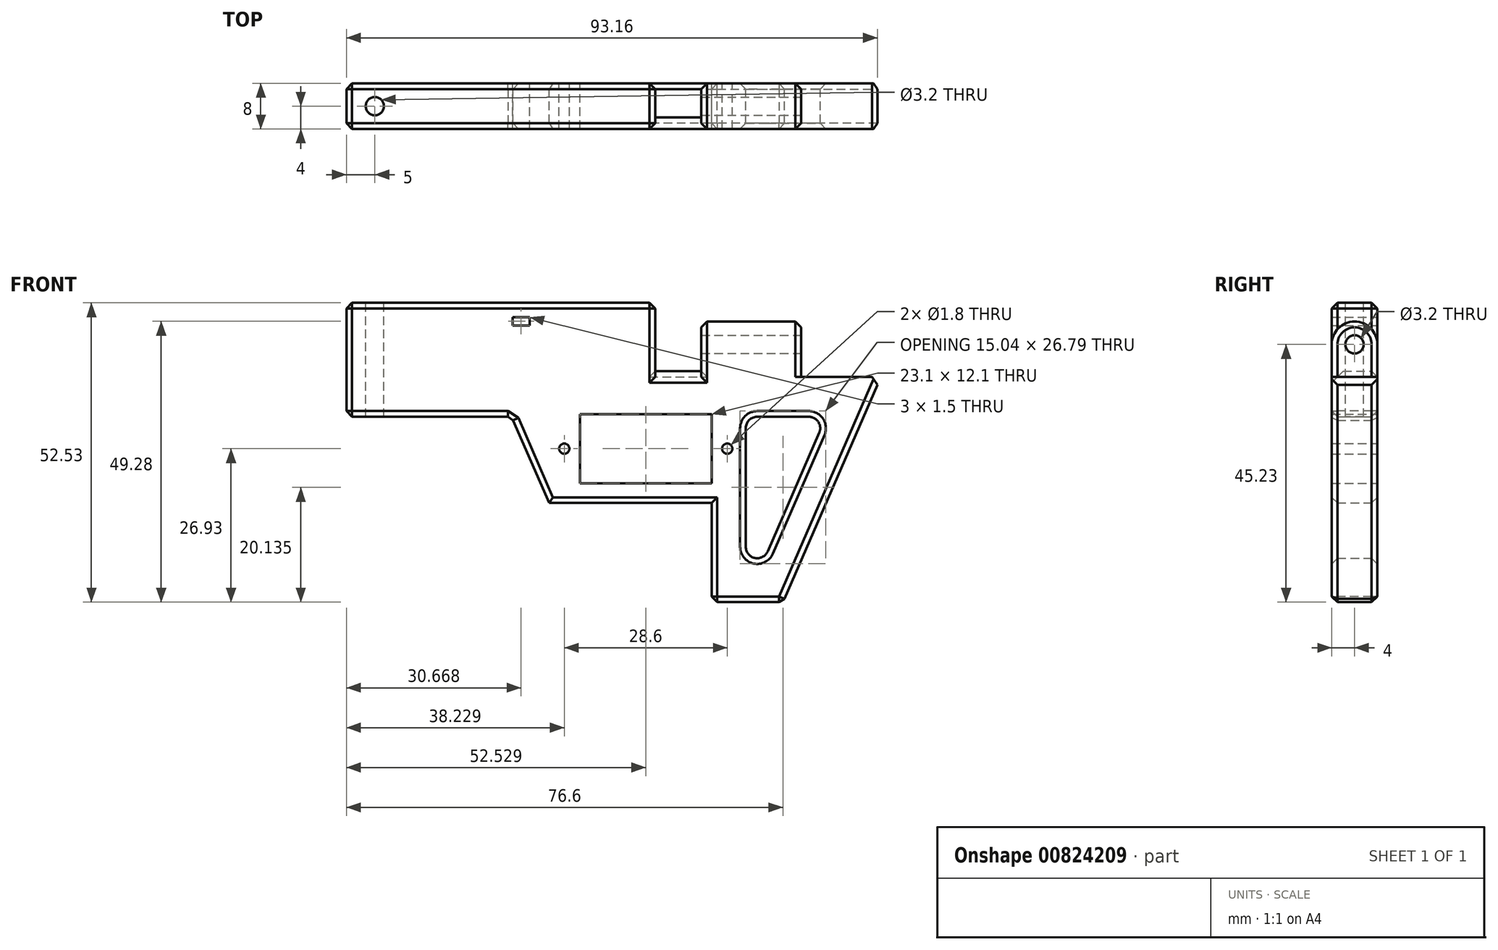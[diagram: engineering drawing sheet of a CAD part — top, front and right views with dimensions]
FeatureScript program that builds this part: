
annotation { "Feature Type Name" : "Feature", "Feature Type Description" : "" }
export const myFeature = defineFeature(function(context is Context, id is Id, definition is map)
    precondition{}
    {
        {
            var Q0;
            Q0=qCreatedBy(makeId("Front.planeOp"),FACE);
            var sketch = newSketch(context, id + "F0", { "sketchPlane" : qUnion([Q0])});
            skLineSegment(sketch, "E0", {"start": v(0, 0) * mm, "end": v(29, 0) * mm});
            skLineSegment(sketch, "E1", {"start": v(29, 0) * mm, "end": v(35.58, -15.13) * mm});
            skLineSegment(sketch, "E2", {"start": v(35.58, -15.13) * mm, "end": v(64.08, -15.13) * mm});
            skLineSegment(sketch, "E3", {"start": v(64.08, -15.13) * mm, "end": v(64.08, -32.53) * mm});
            skLineSegment(sketch, "E4", {"start": v(64.08, -32.53) * mm, "end": v(76.58, -32.53) * mm});
            skLineSegment(sketch, "E5", {"start": v(76.58, -32.53) * mm, "end": v(93.77, 7) * mm});
            skLineSegment(sketch, "E6", {"start": v(79.77, 7) * mm, "end": v(79.77, 16.7) * mm});
            skLineSegment(sketch, "E7", {"start": v(79.77, 16.7) * mm, "end": v(62.27, 16.7) * mm});
            skLineSegment(sketch, "E8", {"start": v(62.27, 16.7) * mm, "end": v(62.27, 8) * mm});
            skLineSegment(sketch, "E9", {"start": v(62.27, 8) * mm, "end": v(54.17, 8) * mm});
            skLineSegment(sketch, "E10", {"start": v(54.17, 8) * mm, "end": v(54.17, 20) * mm});
            skLineSegment(sketch, "E11", {"start": v(54.17, 20) * mm, "end": v(0, 20) * mm});
            skLineSegment(sketch, "E12", {"start": v(0, 20) * mm, "end": v(0, 0) * mm});
            skCircle(sketch, "E13", {"center": v(38.23, -5.6) * mm, "radius": 0.9 * mm});
            skCircle(sketch, "E14", {"center": v(66.83, -5.6) * mm, "radius": 0.9 * mm});
            skLineSegment(sketch, "E15.bottom", {"start": v(40.98, 0.45) * mm, "end": v(64.08, 0.45) * mm});
            skLineSegment(sketch, "E15.top", {"start": v(40.98, -11.65) * mm, "end": v(64.08, -11.65) * mm});
            skLineSegment(sketch, "E15.left", {"start": v(40.98, 0.45) * mm, "end": v(40.98, -11.65) * mm});
            skLineSegment(sketch, "E15.right", {"start": v(64.08, 0.45) * mm, "end": v(64.08, -11.65) * mm});
            skLineSegment(sketch, "E16", {"start": v(70.08, -2) * mm, "end": v(70.08, -22.82) * mm});
            skLineSegment(sketch, "E17", {"start": v(73.91, -23.62) * mm, "end": v(82.97, -2.8) * mm});
            skLineSegment(sketch, "E18", {"start": v(81.13, 0) * mm, "end": v(72.08, 0) * mm});
            skLineSegment(sketch, "E19.bottom", {"start": v(29.17, 17.5) * mm, "end": v(32.17, 17.5) * mm});
            skLineSegment(sketch, "E19.top", {"start": v(29.17, 16) * mm, "end": v(32.17, 16) * mm});
            skLineSegment(sketch, "E19.left", {"start": v(29.17, 17.5) * mm, "end": v(29.17, 16) * mm});
            skLineSegment(sketch, "E19.right", {"start": v(32.17, 17.5) * mm, "end": v(32.17, 16) * mm});
            skPoint(sketch, "E20.visualSharp", {"position": v(84.18, 0) * mm});
            skArc(sketch, "E20.filletArc", {"start": v(82.97, -2.8) * mm, "mid": v(82.8, -0.9) * mm, "end": v(81.13, 0) * mm});
            skPoint(sketch, "E21.visualSharp", {"position": v(70.08, 0) * mm});
            skArc(sketch, "E21.filletArc", {"start": v(72.08, 0) * mm, "mid": v(70.67, -0.59) * mm, "end": v(70.08, -2) * mm});
            skPoint(sketch, "E22.visualSharp", {"position": v(70.08, -32.43) * mm});
            skArc(sketch, "E22.filletArc", {"start": v(70.08, -22.82) * mm, "mid": v(71.67, -24.78) * mm, "end": v(73.91, -23.62) * mm});
            skPoint(sketch, "E23", {"position": v(40.98, -5.6) * mm});
            skLineSegment(sketch, "E24", {"start": v(52.53, 0.45) * mm, "end": v(52.53, -11.65) * mm, "construction": true});
            skLineSegment(sketch, "E25", {"start": v(93.77, 7) * mm, "end": v(79.77, 7) * mm});
            skPoint(sketch, "E26", {"position": v(49.83, -15.13) * mm});
            skSolve(sketch);
        }
        {
            var Q0;
            Q0=makeQuery(id+"F0.imprint","IMPRINT",FACE,{"disambiguationData":[TD([[makeQuery(id+"F0.imprint","IMPRINT",EDGE,{"derivedFrom":sQuery(id+"F0.wireOp",EDGE,"E0")}),1.0]])]});
            extrude(context, id + "F1", {"entities" : qUnion([Q0]), "depth" : 8 * mm, "offsetDistance" : 25 * mm});
        }
        {
            var Q0;
            Q0=makeQuery(id+"F1.opExtrude","SWEPT_FACE",FACE,{"disambiguationData":[OSD([sQuery(id+"F0.wireOp",EDGE,"E6")])]});
            var sketch = newSketch(context, id + "F2", { "sketchPlane" : qUnion([Q0])});
            skCircle(sketch, "E27", {"center": v(-4, 12.7) * mm, "radius": 1.6 * mm});
            skPoint(sketch, "E27.centerSnap0", {"position": v(-4, 16.7) * mm});
            skSolve(sketch);
        }
        {
            var Q0;
            Q0=makeQuery(id+"F2.imprint","IMPRINT",FACE,{"disambiguationData":[TD([[makeQuery(id+"F2.imprint","IMPRINT",EDGE,{"derivedFrom":sQuery(id+"F2.wireOp",EDGE,"E27")}),1.0]])]});
            extrude(context, id + "F3", {"entities" : qUnion([Q0]), "operationType" : NewBodyOperationType.REMOVE, "endBound" : BoundingType.UP_TO_NEXT, "oppositeDirection" : true, "depth" : 25 * mm, "offsetDistance" : 25 * mm});
        }
        {
            var Q0;
            Q0=makeQuery(id+"F1.opExtrude","CAP_EDGE",EDGE,{"disambiguationData":[OSD([sQuery(id+"F0.wireOp",EDGE,"E7")])],"isStart":false});
            var Q1;
            Q1=makeQuery(id+"F1.opExtrude","CAP_EDGE",EDGE,{"disambiguationData":[OSD([sQuery(id+"F0.wireOp",EDGE,"E7")])],"isStart":true});
            fillet(context, id + "F4", {"entities" : qUnion([Q0, Q1]), "radius" : 4 * mm, "tangentPropagation" : true, "allowEdgeOverflow" : false});
        }
        {
            var Q0;
            Q0=makeQuery(id+"F1.opExtrude","SWEPT_FACE",FACE,{"disambiguationData":[OSD([sQuery(id+"F0.wireOp",EDGE,"E11")])]});
            var sketch = newSketch(context, id + "F5", { "sketchPlane" : qUnion([Q0])});
            skCircle(sketch, "E28", {"center": v(5, -4) * mm, "radius": 1.6 * mm});
            skPoint(sketch, "E28.centerSnap0", {"position": v(0, -4) * mm});
            skSolve(sketch);
        }
        {
            var Q0;
            Q0 = qSketchRegion(id + "F5", true);
            extrude(context, id + "F6", {"entities" : qUnion([Q0]), "operationType" : NewBodyOperationType.REMOVE, "endBound" : BoundingType.UP_TO_NEXT, "oppositeDirection" : true, "depth" : 25 * mm, "offsetDistance" : 25 * mm});
        }
        {
            var Q0;
            Q0=makeQuery(id+"F1.opExtrude","CAP_EDGE",EDGE,{"disambiguationData":[OSD([sQuery(id+"F0.wireOp",EDGE,"E11")])],"isStart":true});
            var Q1;
            Q1=makeQuery(id+"F1.opExtrude","CAP_EDGE",EDGE,{"disambiguationData":[OSD([sQuery(id+"F0.wireOp",EDGE,"E10")])],"isStart":true});
            var Q2;
            Q2=makeQuery(id+"F1.opExtrude","CAP_EDGE",EDGE,{"disambiguationData":[OSD([sQuery(id+"F0.wireOp",EDGE,"E9")])],"isStart":true});
            var Q3;
            Q3=makeQuery(id+"F1.opExtrude","CAP_EDGE",EDGE,{"disambiguationData":[OSD([sQuery(id+"F0.wireOp",EDGE,"E8")])],"isStart":true});
            var Q4;
            Q4=makeQuery(id+"F1.opExtrude","CAP_EDGE",EDGE,{"disambiguationData":[OSD([sQuery(id+"F0.wireOp",EDGE,"E6")])],"isStart":true});
            var Q5;
            Q5=makeQuery(id+"F1.opExtrude","CAP_EDGE",EDGE,{"disambiguationData":[OSD([sQuery(id+"F0.wireOp",EDGE,"ISF7o4jE-YCiz-FvaA-wAcF-tz2zpi0BwcWr")])],"isStart":true});
            var Q6;
            Q6=makeQuery(id+"F1.opExtrude","CAP_EDGE",EDGE,{"disambiguationData":[OSD([sQuery(id+"F0.wireOp",EDGE,"E5")])],"isStart":false});
            var Q7;
            Q7=makeQuery(id+"F1.opExtrude","CAP_EDGE",EDGE,{"disambiguationData":[OSD([sQuery(id+"F0.wireOp",EDGE,"E17")])],"isStart":true});
            var Q8;
            Q8=makeQuery(id+"F1.opExtrude","CAP_EDGE",EDGE,{"disambiguationData":[OSD([sQuery(id+"F0.wireOp",EDGE,"E4")])],"isStart":true});
            var Q9;
            Q9=makeQuery(id+"F1.opExtrude","CAP_EDGE",EDGE,{"disambiguationData":[OSD([sQuery(id+"F0.wireOp",EDGE,"E2")])],"isStart":true});
            var Q10;
            Q10=makeQuery(id+"F1.opExtrude","CAP_EDGE",EDGE,{"disambiguationData":[OSD([sQuery(id+"F0.wireOp",EDGE,"E3")])],"isStart":true});
            var Q11;
            Q11=makeQuery(id+"F1.opExtrude","CAP_EDGE",EDGE,{"disambiguationData":[OSD([sQuery(id+"F0.wireOp",EDGE,"E1")])],"isStart":true});
            var Q12;
            Q12=makeQuery(id+"F1.opExtrude","CAP_EDGE",EDGE,{"disambiguationData":[OSD([sQuery(id+"F0.wireOp",EDGE,"E0")])],"isStart":true});
            var Q13;
            Q13=makeQuery(id+"F1.opExtrude","CAP_EDGE",EDGE,{"disambiguationData":[OSD([sQuery(id+"F0.wireOp",EDGE,"E12")])],"isStart":true});
            var Q14;
            Q14=makeQuery(id+"F1.opExtrude","SWEPT_EDGE",EDGE,{"disambiguationData":[OSD([sQuery(id+"F0.wireOp",EDGE,"E4"),sQuery(id+"F0.wireOp",EDGE,"E5")])]});
            var Q15;
            Q15=makeQuery(id+"F1.opExtrude","CAP_EDGE",EDGE,{"disambiguationData":[OSD([sQuery(id+"F0.wireOp",EDGE,"E4")])],"isStart":false});
            var Q16;
            Q16=makeQuery(id+"F1.opExtrude","SWEPT_EDGE",EDGE,{"disambiguationData":[OSD([sQuery(id+"F0.wireOp",EDGE,"E3"),sQuery(id+"F0.wireOp",EDGE,"E4")])]});
            var Q17;
            Q17=makeQuery(id+"F1.opExtrude","CAP_EDGE",EDGE,{"disambiguationData":[OSD([sQuery(id+"F0.wireOp",EDGE,"E3")])],"isStart":false});
            var Q18;
            Q18=makeQuery(id+"F1.opExtrude","CAP_EDGE",EDGE,{"disambiguationData":[OSD([sQuery(id+"F0.wireOp",EDGE,"E2")])],"isStart":false});
            var Q19;
            Q19=makeQuery(id+"F1.opExtrude","CAP_EDGE",EDGE,{"disambiguationData":[OSD([sQuery(id+"F0.wireOp",EDGE,"E1")])],"isStart":false});
            var Q20;
            Q20=makeQuery(id+"F1.opExtrude","CAP_EDGE",EDGE,{"disambiguationData":[OSD([sQuery(id+"F0.wireOp",EDGE,"E0")])],"isStart":false});
            var Q21;
            Q21=makeQuery(id+"F1.opExtrude","SWEPT_EDGE",EDGE,{"disambiguationData":[OSD([sQuery(id+"F0.wireOp",EDGE,"E0"),sQuery(id+"F0.wireOp",EDGE,"E1")])]});
            var Q22;
            Q22=makeQuery(id+"F1.opExtrude","CAP_EDGE",EDGE,{"disambiguationData":[OSD([sQuery(id+"F0.wireOp",EDGE,"E12")])],"isStart":false});
            var Q23;
            Q23=makeQuery(id+"F1.opExtrude","SWEPT_EDGE",EDGE,{"disambiguationData":[OSD([sQuery(id+"F0.wireOp",EDGE,"E0"),sQuery(id+"F0.wireOp",EDGE,"E12")])]});
            var Q24;
            Q24=makeQuery(id+"F1.opExtrude","SWEPT_EDGE",EDGE,{"disambiguationData":[OSD([sQuery(id+"F0.wireOp",EDGE,"E11"),sQuery(id+"F0.wireOp",EDGE,"E12")])]});
            var Q25;
            Q25=makeQuery(id+"F1.opExtrude","CAP_EDGE",EDGE,{"disambiguationData":[OSD([sQuery(id+"F0.wireOp",EDGE,"E11")])],"isStart":false});
            var Q26;
            Q26=makeQuery(id+"F1.opExtrude","SWEPT_EDGE",EDGE,{"disambiguationData":[OSD([sQuery(id+"F0.wireOp",EDGE,"E10"),sQuery(id+"F0.wireOp",EDGE,"E11")])]});
            var Q27;
            Q27=makeQuery(id+"F1.opExtrude","CAP_EDGE",EDGE,{"disambiguationData":[OSD([sQuery(id+"F0.wireOp",EDGE,"E10")])],"isStart":false});
            var Q28;
            Q28=makeQuery(id+"F1.opExtrude","CAP_EDGE",EDGE,{"disambiguationData":[OSD([sQuery(id+"F0.wireOp",EDGE,"E16")])],"isStart":false});
            var Q29;
            Q29=makeQuery(id+"F1.opExtrude","CAP_EDGE",EDGE,{"disambiguationData":[OSD([sQuery(id+"F0.wireOp",EDGE,"ISF7o4jE-YCiz-FvaA-wAcF-tz2zpi0BwcWr")])],"isStart":false});
            var Q30;
            Q30=makeQuery(id+"F1.opExtrude","SWEPT_EDGE",EDGE,{"disambiguationData":[OSD([sQuery(id+"F0.wireOp",EDGE,"E5"),sQuery(id+"F0.wireOp",EDGE,"ISF7o4jE-YCiz-FvaA-wAcF-tz2zpi0BwcWr")])]});
            var Q31;
            Q31=makeQuery(id+"F1.opExtrude","CAP_EDGE",EDGE,{"disambiguationData":[OSD([sQuery(id+"F0.wireOp",EDGE,"E5")])],"isStart":true});
            chamfer(context, id + "F7", {"entities" : qUnion([Q0, Q1, Q2, Q3, Q4, Q5, Q6, Q7, Q8, Q9, Q10, Q11, Q12, Q13, Q14, Q15, Q16, Q17, Q18, Q19, Q20, Q21, Q22, Q23, Q24, Q25, Q26, Q27, Q28, Q29, Q30, Q31]), "width" : 1 * mm, "tangentPropagation" : true});
        }
        {
            var Q0;
            Q0=makeQuery(id+"F1.opExtrude","CAP_EDGE",EDGE,{"disambiguationData":[OSD([sQuery(id+"F0.wireOp",EDGE,"E9")])],"isStart":false});
            chamfer(context, id + "F8", {"entities" : qUnion([Q0]), "width" : 2 * mm, "tangentPropagation" : true});
        }
    });
